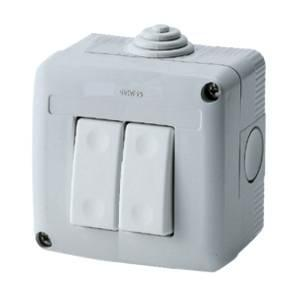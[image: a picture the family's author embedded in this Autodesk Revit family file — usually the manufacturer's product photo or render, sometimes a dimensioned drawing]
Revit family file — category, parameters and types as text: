
# Revit family: Domotics-SerieCivili-GEWISS-27COMBI_SYSTEM-IP40_COMANDO_1M
name_source: partatom
category: Apparecchi elettrici
revit_build: Autodesk Revit 2016 (Build: 20161004_0715(x64)
units: mm (PartAtom-declared; Revit-internal decimal feet)

## family parameters
Condiviso = Sì
Host = Superficie
Mantenere orientamento annotazione = Sì
Numero OmniClass = 23.80.50.11.14
Punto di calcolo locali = No
Quota connettore circolare = Usa diametro
Taglio con vuoti quando caricato = Sì
Tipo di parte = Normale
Titolo OmniClass = Switches

## types (1)
- Domotics-SerieCivili-GEWISS-27COMBI_SYSTEM-IP40_COMANDO_1M
    1DEV = Sì
    2DEV = No
    Bidimensionale = bidimensionale system contenitori IP40 completi pulsanti : 1P
    Caratteristiche = Halogen free
    Catalogo = DOMOTICS
    Catalogo Serie = 27COMBI
    Classe isolamento = II
    Codice EAN = 8011564095380
    Codice Electrocod = 0130
    Colore = Grigio RAL 7035
    Contenitore = SYSTEM CONTENITORI IP40_BASE : GW27001 - 1 posto
    Coppia serraggio viti = 0,8NM
    Descrizione = PULSANTE UNIP.10A PROTETTO
    Descrizione: = Pulsante 1P NA - 10 A
    Dim. esterne BxHxP (mm) = 66x82x55
    Dimensioni BxHxP (mm) = 66x82x55
    Glow Wire Test = 650°C
    Grado di protezione = IP40
    IDF = 73c6b23c-00ac-4ee6-9d94-9eeb7a2c470f
    IDT = 264e3860-11d5-4595-8a4f-1cc7c44a1a4c
    INT = No
    Immagine tipo = GW27805.jpg
    Larghezza foro = 23 mm  [stored 0.0754593 ft]
    Larghezza scatola = 66 mm  [stored 0.216535 ft]
    Modello = GW27805
    N. fori Ã˜ 23 con passacavo = 1
    N. fori Ã˜ 23 sfondabili = 3
    N. fori Ã˜ 23 sfondabili: = Laterali 3 / Sul fondo 1
    Norma di riferimento: = EN 60669-1
    Produttore = GEWISS S.p.A.
    Prospetto di default = 1219 mm
    SCATOLA = GEWISS GRIGIO
    SEO = Contenitore
    Scheda Tecnica = https://www.gewiss.com
    Simbolo = SIMBOLO CONTENITORI COMPLETI : PUL
    Temperatura di installazione = -25 +60 °C
    Tensione = 230 V ac
    Tensione: = 250 V ac
    Termopressione con biglia = 70 °C
    Tipo Deviatore = SYSTEM DEVIATORI_BASE : GW20576 - DEVIATORE 1P 16AX SY/WT
    Tipo interruttore = SYSTEM INTERRUTTORI_BASE : GW20503 - INTERRUTTORE 2P 16A SY/WT - 0 / 1
    Tipo sfondabili = Asportabili con utensile
    URL = https://www.gewiss.com
    Versione file RFA = 19.4
    Viti coperchio = Acciaio resistente alla corrosione

note: [stored X ft] marks values corroborated as IEEE doubles in the binary element streams (Revit-internal decimal feet)

## geometry (parser evidence)
native form markers: Sweep x2
no freeform markers — native parametric forms only
